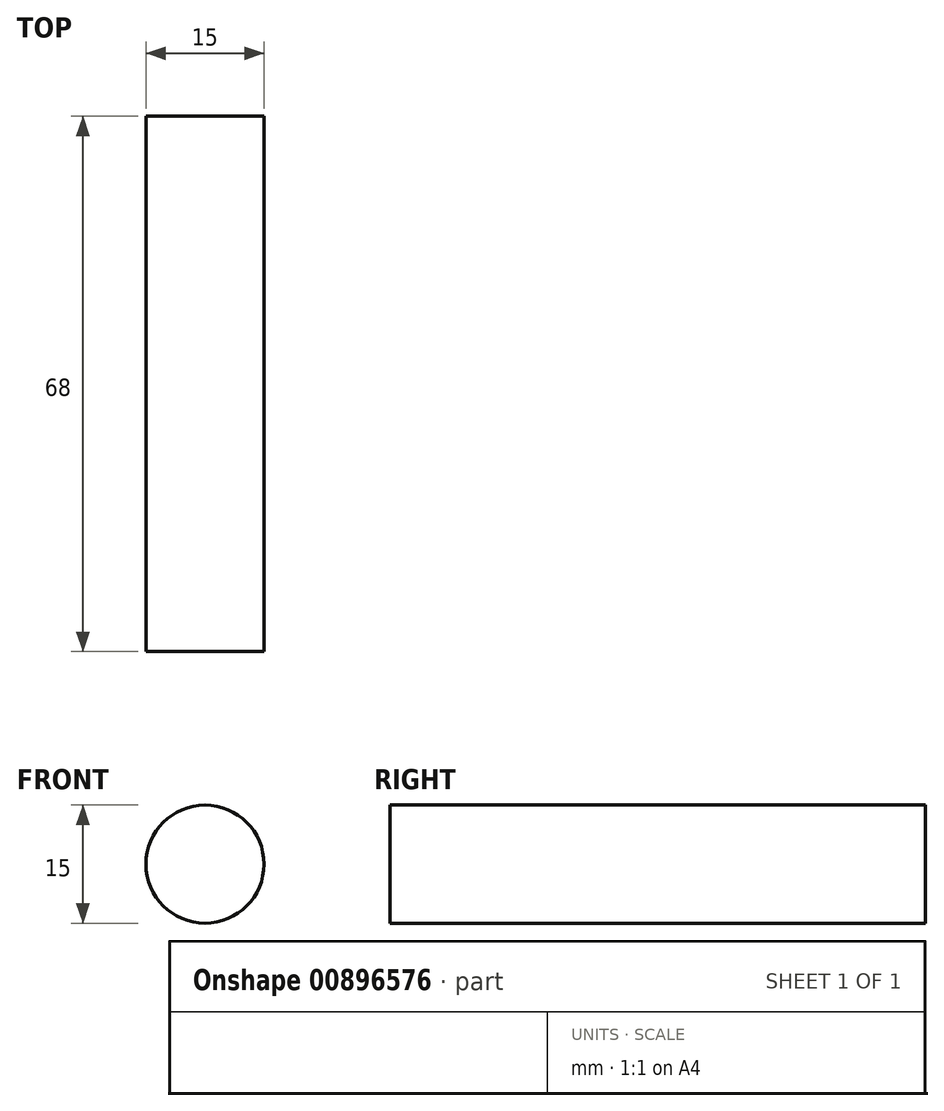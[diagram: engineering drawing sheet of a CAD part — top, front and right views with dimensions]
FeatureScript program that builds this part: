
annotation { "Feature Type Name" : "Feature", "Feature Type Description" : "" }
export const myFeature = defineFeature(function(context is Context, id is Id, definition is map)
    precondition{}
    {
        {
            var Q0;
            Q0=qCreatedBy(makeId("Front.planeOp"),FACE);
            var sketch = newSketch(context, id + "F0", { "sketchPlane" : qUnion([Q0])});
            skCircle(sketch, "E0", {"center": v(0, 0) * mm, "radius": 7.5 * mm});
            skSolve(sketch);
        }
        {
            var Q0;
            Q0 = qSketchRegion(id + "F0", true);
            extrude(context, id + "F1", {"entities" : qUnion([Q0]), "endBound" : BoundingType.SYMMETRIC, "depth" : 68 * mm, "offsetDistance" : 25 * mm});
        }
    });
